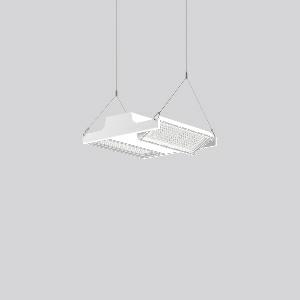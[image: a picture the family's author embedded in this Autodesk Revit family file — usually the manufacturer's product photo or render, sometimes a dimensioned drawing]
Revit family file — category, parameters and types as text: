
# Revit family: light_case_921680_002_1_76_cb47
name_source: partatom
category: Lighting Fixtures
units: mm (PartAtom-declared; Revit-internal decimal feet)

## family parameters
Cut with Voids When Loaded = No
Host = Face
Light Source = No
Part Type = Normal
Room Calculation Point = No
Round Connector Dimension = Use Diameter
Shared = No

## types (1)
- LIGHT CASE (1 x LED Modul 865, 8650 lm, 6500)
    Apparent Load = 117 VA
    CIE Flux Codes = 88 95 99 100 100
    Color Rendering = 80
    Color Temperature = 6500
    Default Elevation = 1800 mm
    Description = Series: LIGHT CASE
Flat highbay luminaire for chain or cable suspension with 2 LED modules that can be swivelled. Housing: die cast aluminium and sheet steel, powder-coated. Optimised thermal management thanks to special luminaire design. Self-cleaning heat sink for constant heat dissipation. Cover: plastic (polycarbonate, shockproof), with integrated four-row lens system. LED modules can be swivelled ± 30° for optimum illumination. Suitable for chain or steel cable suspension (to be provided on site). With 5-pin connection terminal (1.5 m). With integrated movement sensor and light sensor for daylight detection on request. Ball impact proof in accordance with DIN 18032-03 (except steel cable suspension). Luminaire with limited surface temperature in accordance with EN 60598-2-24 for use in environments in which a deposit of conductive dust on the luminaire can be expected. 
Colour: white
Length: 406 mm
Width: 397 mm
Height: 110 mm
Lamp: LED
Socket: without socket
Colour temperature: 6500K
Colour rendering index (CRI): 80
System power: 117 W
Rated luminous flux: 17300 lm
Luminous efficiency: 148 lm/W
Control gear: Converter, dimmable, DALI
Protection class: I
Type of protection: IP 65
    Height = 110 mm
    Lamp = 1 x LED Modul 865
    Lamp Light Flux = 8650 lm
    Lamp count = 1
    Length = 406 mm
    Lifetime = 50000 h
    Luminous efficacy = 148 lm/W
    Manufacturer = RZB
    ModVariant = No
    Model = 921680.002.1.76
    Mounting Place = Ceiling
    Mounting Type = Pendant
    Number of Poles = 1
    OnlyDefault = Yes
    Power Factor = 1
    Product Name = LIGHT CASE
    Product group = Pendant commercial luminaires
    ProductGroupID = 903
    Protection Class = Protection class I
    Protection Degree = IP 65
    RLX_Detail_Level = 1
    RLX_Emergency_Light_Flux = 0 lm
    RLX_Emergency_Type = 0
    RLX_Emergency_Type_DB = No
    RlxData = <blob elided: 25825 chars, md5=bce2805b>
    Socket = socket
    Standby Power = 0 W
    System Light Flux = 17300 lm
    System Power = 117 W
    Type Comments = Product without accessories
    Type Image = 921517.002.76.jpg
    URL = http://relux.com
    VarID = ---
    Voltage = 230 V
    Voltage Range = 220-240 V
    Weight = 0.00 kg
    Width = 397 mm

## geometry (parser evidence)
native form markers: Blend x4, Sweep x17
no freeform markers — native parametric forms only
